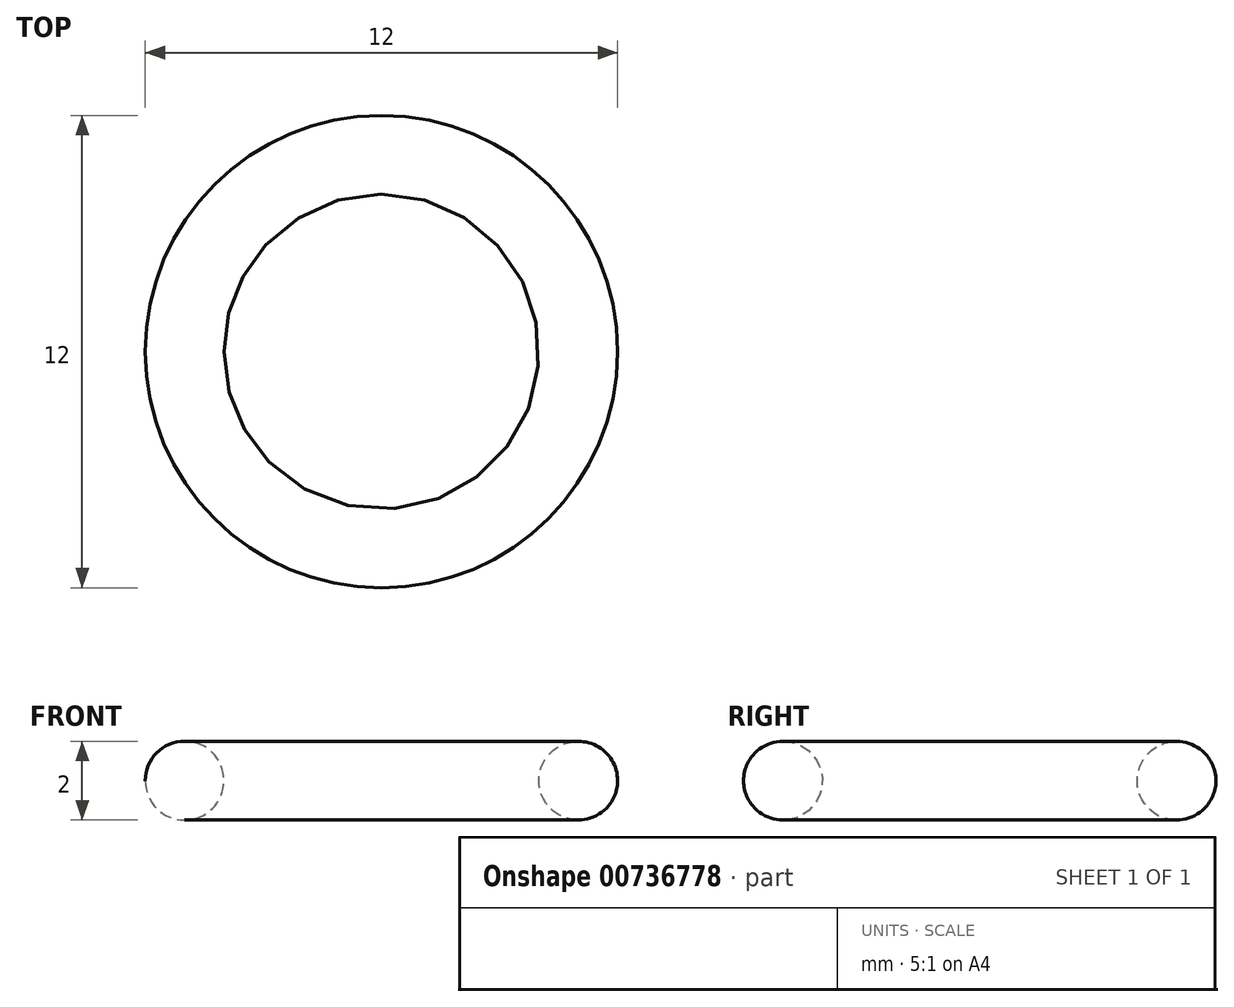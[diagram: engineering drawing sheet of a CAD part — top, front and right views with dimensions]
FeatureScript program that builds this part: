
annotation { "Feature Type Name" : "Feature", "Feature Type Description" : "" }
export const myFeature = defineFeature(function(context is Context, id is Id, definition is map)
    precondition{}
    {
        {
            var Q0;
            Q0=qCreatedBy(makeId("Top.planeOp"),FACE);
            var sketch = newSketch(context, id + "F0", { "sketchPlane" : qUnion([Q0])});
            skCircle(sketch, "E0", {"center": v(0, 0) * mm, "radius": 5 * mm});
            skSolve(sketch);
        }
        {
            var Q0;
            Q0=qCreatedBy(makeId("Front.planeOp"),FACE);
            var sketch = newSketch(context, id + "F1", { "sketchPlane" : qUnion([Q0])});
            skCircle(sketch, "E1", {"center": v(5, 0) * mm, "radius": 1 * mm});
            skSolve(sketch);
        }
        {
            var Q0;
            Q0=makeQuery(id+"F1.imprint","IMPRINT",FACE,{"disambiguationData":[TD([[makeQuery(id+"F1.imprint","IMPRINT",EDGE,{"derivedFrom":sQuery(id+"F1.wireOp",EDGE,"E1")}),1.0]])]});
            var Q1;
            Q1=sQuery(id+"F0.wireOp",EDGE,"E0");
            revolve(context, id + "F2", {"surfaceOperationType" : NewSurfaceOperationType.NEW, "entities" : qUnion([Q0]), "axis" : qUnion([Q1]), "revolveType" : RevolveType.FULL});
        }
    });
